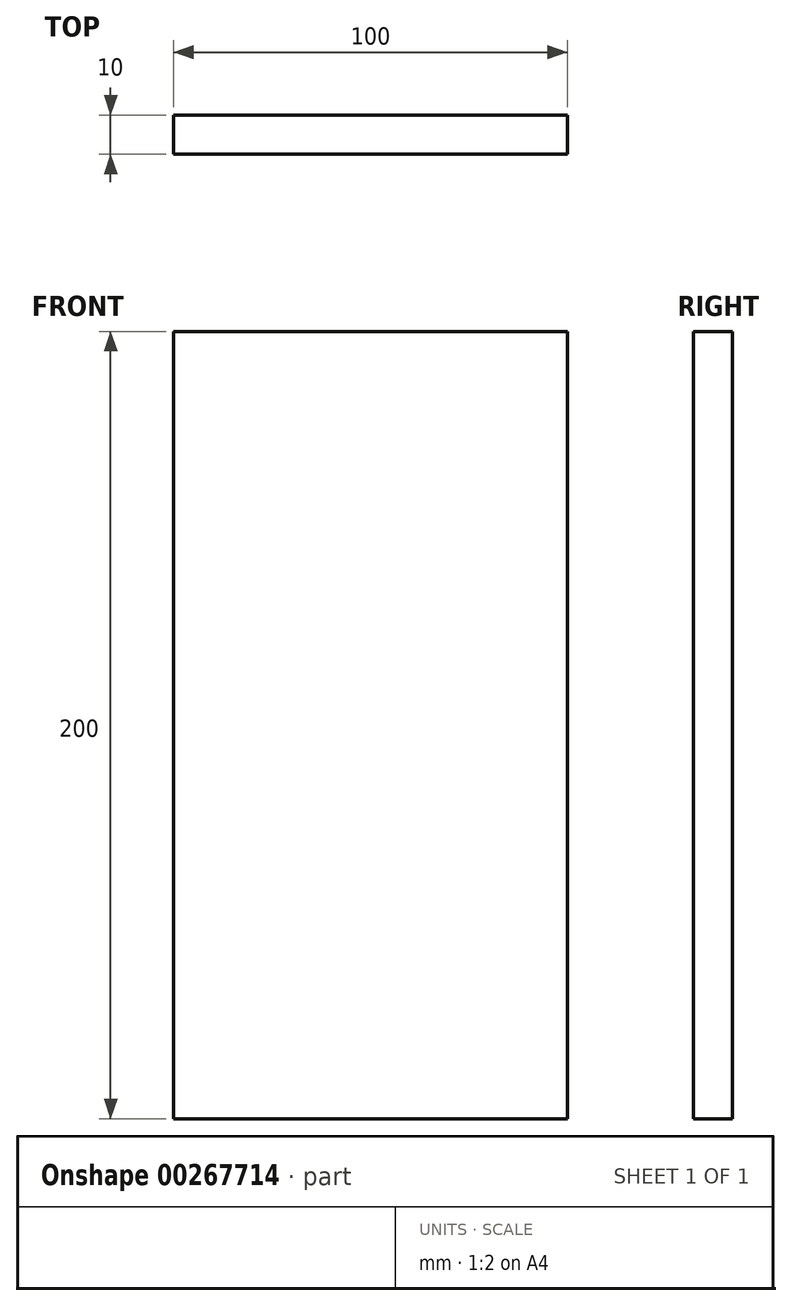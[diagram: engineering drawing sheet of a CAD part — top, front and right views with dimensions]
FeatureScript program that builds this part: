
annotation { "Feature Type Name" : "Feature", "Feature Type Description" : "" }
export const myFeature = defineFeature(function(context is Context, id is Id, definition is map)
    precondition{}
    {
        {
            var Q0;
            Q0=qCreatedBy(makeId("Front.planeOp"),FACE);
            var sketch = newSketch(context, id + "F0", { "sketchPlane" : qUnion([Q0])});
            skLineSegment(sketch, "E0.bottom", {"start": v(50, 100) * mm, "end": v(-50, 100) * mm});
            skLineSegment(sketch, "E0.top", {"start": v(50, -100) * mm, "end": v(-50, -100) * mm});
            skLineSegment(sketch, "E0.left", {"start": v(50, 100) * mm, "end": v(50, -100) * mm});
            skLineSegment(sketch, "E0.right", {"start": v(-50, 100) * mm, "end": v(-50, -100) * mm});
            skPoint(sketch, "E0.middle", {"position": v(0, 0) * mm});
            skSolve(sketch);
        }
        {
            var Q0;
            Q0=makeQuery(id+"F0.imprint","IMPRINT",FACE,{"disambiguationData":[TD([[makeQuery(id+"F0.imprint","IMPRINT",EDGE,{"derivedFrom":sQuery(id+"F0.wireOp",EDGE,"E0.bottom")}),1.0]])]});
            extrude(context, id + "F1", {"entities" : qUnion([Q0]), "oppositeDirection" : true, "depth" : 10 * mm});
        }
    });
